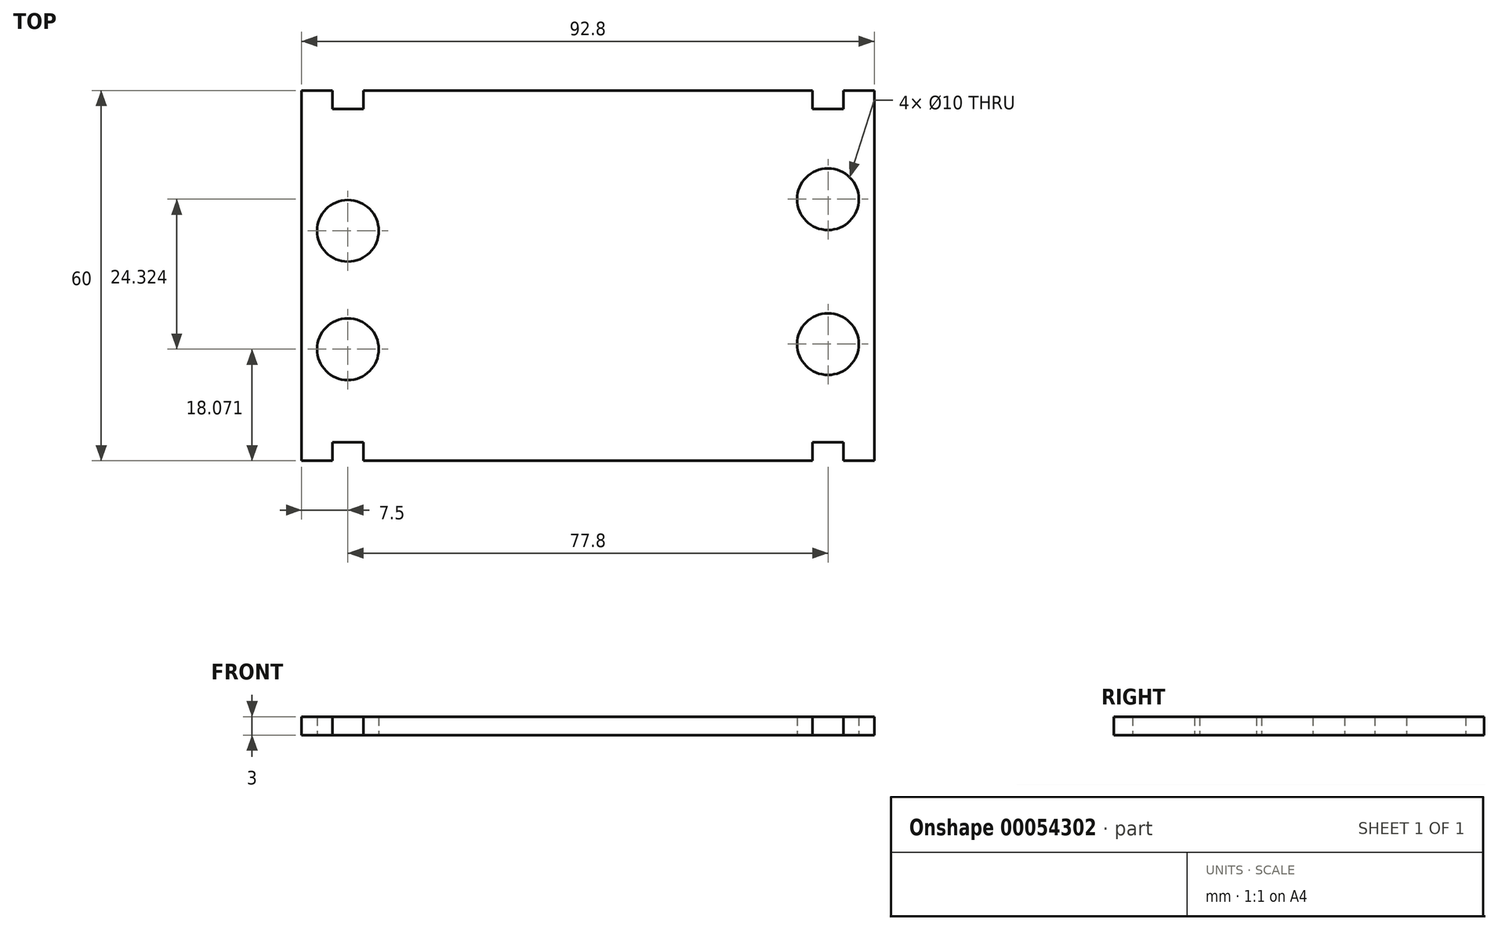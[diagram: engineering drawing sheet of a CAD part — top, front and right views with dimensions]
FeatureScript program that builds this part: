
annotation { "Feature Type Name" : "Feature", "Feature Type Description" : "" }
export const myFeature = defineFeature(function(context is Context, id is Id, definition is map)
    precondition{}
    {
        {
            var Q0;
            Q0=qCreatedBy(makeId("Top.planeOp"),FACE);
            var sketch = newSketch(context, id + "F0", { "sketchPlane" : qUnion([Q0])});
            skLineSegment(sketch, "E0.rect.bottom", {"start": v(92.8, 0) * mm, "end": v(0, 0) * mm});
            skLineSegment(sketch, "E0.rect.top", {"start": v(92.8, -60) * mm, "end": v(0, -60) * mm});
            skLineSegment(sketch, "E0.rect.left", {"start": v(92.8, 0) * mm, "end": v(92.8, -60) * mm});
            skLineSegment(sketch, "E0.rect.right", {"start": v(0, 0) * mm, "end": v(0, -60) * mm});
            skLineSegment(sketch, "E1.bottom", {"start": v(5, 0) * mm, "end": v(10, 0) * mm});
            skLineSegment(sketch, "E1.top", {"start": v(5, -3) * mm, "end": v(10, -3) * mm});
            skLineSegment(sketch, "E1.left", {"start": v(5, 0) * mm, "end": v(5, -3) * mm});
            skLineSegment(sketch, "E1.right", {"start": v(10, 0) * mm, "end": v(10, -3) * mm});
            skLineSegment(sketch, "E2.bottom", {"start": v(82.8, 0) * mm, "end": v(87.8, 0) * mm});
            skLineSegment(sketch, "E2.top", {"start": v(82.8, -3) * mm, "end": v(87.8, -3) * mm});
            skLineSegment(sketch, "E2.left", {"start": v(82.8, 0) * mm, "end": v(82.8, -3) * mm});
            skLineSegment(sketch, "E2.right", {"start": v(87.8, 0) * mm, "end": v(87.8, -3) * mm});
            skLineSegment(sketch, "E3.bottom", {"start": v(5, -60) * mm, "end": v(10, -60) * mm});
            skLineSegment(sketch, "E3.top", {"start": v(5, -57) * mm, "end": v(10, -57) * mm});
            skLineSegment(sketch, "E3.left", {"start": v(5, -60) * mm, "end": v(5, -57) * mm});
            skLineSegment(sketch, "E3.right", {"start": v(10, -60) * mm, "end": v(10, -57) * mm});
            skLineSegment(sketch, "E4.bottom", {"start": v(82.8, -60) * mm, "end": v(87.8, -60) * mm});
            skLineSegment(sketch, "E4.top", {"start": v(82.8, -57) * mm, "end": v(87.8, -57) * mm});
            skLineSegment(sketch, "E4.left", {"start": v(82.8, -60) * mm, "end": v(82.8, -57) * mm});
            skLineSegment(sketch, "E4.right", {"start": v(87.8, -60) * mm, "end": v(87.8, -57) * mm});
            skLineSegment(sketch, "E5", {"start": v(15, 0) * mm, "end": v(15, -60) * mm, "construction": true});
            skLineSegment(sketch, "E6", {"start": v(77.8, 0) * mm, "end": v(77.8, -60) * mm, "construction": true});
            skLineSegment(sketch, "E7", {"start": v(15, -60) * mm, "end": v(15, -3) * mm});
            skLineSegment(sketch, "E8", {"start": v(16.9, 0) * mm, "end": v(16.9, -57) * mm});
            skLineSegment(sketch, "E9.1.0.0", {"start": v(18.8, -60) * mm, "end": v(18.8, -3) * mm});
            skLineSegment(sketch, "E9.1.0.1", {"start": v(20.7, 0) * mm, "end": v(20.7, -57) * mm});
            skLineSegment(sketch, "E9.2.0.0", {"start": v(22.6, -60) * mm, "end": v(22.6, -3) * mm});
            skLineSegment(sketch, "E9.2.0.1", {"start": v(24.5, 0) * mm, "end": v(24.5, -57) * mm});
            skLineSegment(sketch, "E9.3.0.0", {"start": v(26.4, -60) * mm, "end": v(26.4, -3) * mm});
            skLineSegment(sketch, "E9.3.0.1", {"start": v(28.3, 0) * mm, "end": v(28.3, -57) * mm});
            skLineSegment(sketch, "E9.4.0.0", {"start": v(30.2, -60) * mm, "end": v(30.2, -3) * mm});
            skLineSegment(sketch, "E9.4.0.1", {"start": v(32.1, 0) * mm, "end": v(32.1, -57) * mm});
            skLineSegment(sketch, "E9.5.0.0", {"start": v(34, -60) * mm, "end": v(34, -3) * mm});
            skLineSegment(sketch, "E9.5.0.1", {"start": v(35.9, 0) * mm, "end": v(35.9, -57) * mm});
            skLineSegment(sketch, "E9.6.0.0", {"start": v(37.8, -60) * mm, "end": v(37.8, -3) * mm});
            skLineSegment(sketch, "E9.6.0.1", {"start": v(39.7, 0) * mm, "end": v(39.7, -57) * mm});
            skLineSegment(sketch, "E9.direction1", {"start": v(15, -60) * mm, "end": v(18.8, -60) * mm, "construction": true});
            skLineSegment(sketch, "E10.0.7.0", {"start": v(41.6, -60) * mm, "end": v(41.6, -3) * mm});
            skLineSegment(sketch, "E10.3.7.0", {"start": v(43.5, 0) * mm, "end": v(43.5, -57) * mm});
            skLineSegment(sketch, "E10.0.8.0", {"start": v(45.4, -60) * mm, "end": v(45.4, -3) * mm});
            skLineSegment(sketch, "E10.3.8.0", {"start": v(47.3, 0) * mm, "end": v(47.3, -57) * mm});
            skLineSegment(sketch, "E10.0.9.0", {"start": v(49.2, -60) * mm, "end": v(49.2, -3) * mm});
            skLineSegment(sketch, "E10.3.9.0", {"start": v(51.1, 0) * mm, "end": v(51.1, -57) * mm});
            skLineSegment(sketch, "E10.0.10.0", {"start": v(53, -60) * mm, "end": v(53, -3) * mm});
            skLineSegment(sketch, "E10.3.10.0", {"start": v(54.9, 0) * mm, "end": v(54.9, -57) * mm});
            skLineSegment(sketch, "E10.0.11.0", {"start": v(56.8, -60) * mm, "end": v(56.8, -3) * mm});
            skLineSegment(sketch, "E10.3.11.0", {"start": v(58.7, 0) * mm, "end": v(58.7, -57) * mm});
            skLineSegment(sketch, "E10.0.12.0", {"start": v(60.6, -60) * mm, "end": v(60.6, -3) * mm});
            skLineSegment(sketch, "E10.3.12.0", {"start": v(62.5, 0) * mm, "end": v(62.5, -57) * mm});
            skLineSegment(sketch, "E10.0.13.0", {"start": v(64.4, -60) * mm, "end": v(64.4, -3) * mm});
            skLineSegment(sketch, "E10.3.13.0", {"start": v(66.3, 0) * mm, "end": v(66.3, -57) * mm});
            skLineSegment(sketch, "E10.0.14.0", {"start": v(68.2, -60) * mm, "end": v(68.2, -3) * mm});
            skLineSegment(sketch, "E10.3.14.0", {"start": v(70.1, 0) * mm, "end": v(70.1, -57) * mm});
            skLineSegment(sketch, "E10.0.15.0", {"start": v(72, -60) * mm, "end": v(72, -3) * mm});
            skLineSegment(sketch, "E10.3.15.0", {"start": v(73.9, 0) * mm, "end": v(73.9, -57) * mm});
            skLineSegment(sketch, "E11.0.16.0", {"start": v(75.8, -60) * mm, "end": v(75.8, -3) * mm});
            skLineSegment(sketch, "E11.3.16.0", {"start": v(77.7, 0) * mm, "end": v(77.7, -57) * mm});
            skCircle(sketch, "E12", {"center": v(7.5, -22.73) * mm, "radius": 5 * mm});
            skCircle(sketch, "E13", {"center": v(7.5, -41.93) * mm, "radius": 5 * mm});
            skCircle(sketch, "E14", {"center": v(85.3, -17.6) * mm, "radius": 5 * mm});
            skCircle(sketch, "E15", {"center": v(85.3, -41.1) * mm, "radius": 5 * mm});
            skCircle(sketch, "E16", {"center": v(7.5, -22.73) * mm, "radius": 1.75 * mm});
            skCircle(sketch, "E17", {"center": v(85.3, -17.6) * mm, "radius": 1.75 * mm});
            skPoint(sketch, "E18", {"position": v(85.3, -3) * mm});
            skPoint(sketch, "E19", {"position": v(85.3, -57) * mm});
            skPoint(sketch, "E20", {"position": v(7.5, -57) * mm});
            skPoint(sketch, "E21", {"position": v(7.5, -3) * mm});
            skSolve(sketch);
        }
        {
            var Q0;
            {var subQ27=sQuery(id+"F0.wireOp",EDGE,"E0.rect.left");Q0=makeQuery(id+"F0.imprint","IMPRINT",FACE,{"disambiguationData":[TD([[makeQuery(id+"F0.imprint","IMPRINT",EDGE,{"derivedFrom":subQ27}),-1.0]])]});}
            extrude(context, id + "F1", {"entities" : qUnion([Q0]), "depth" : 3 * mm});
        }
    });
